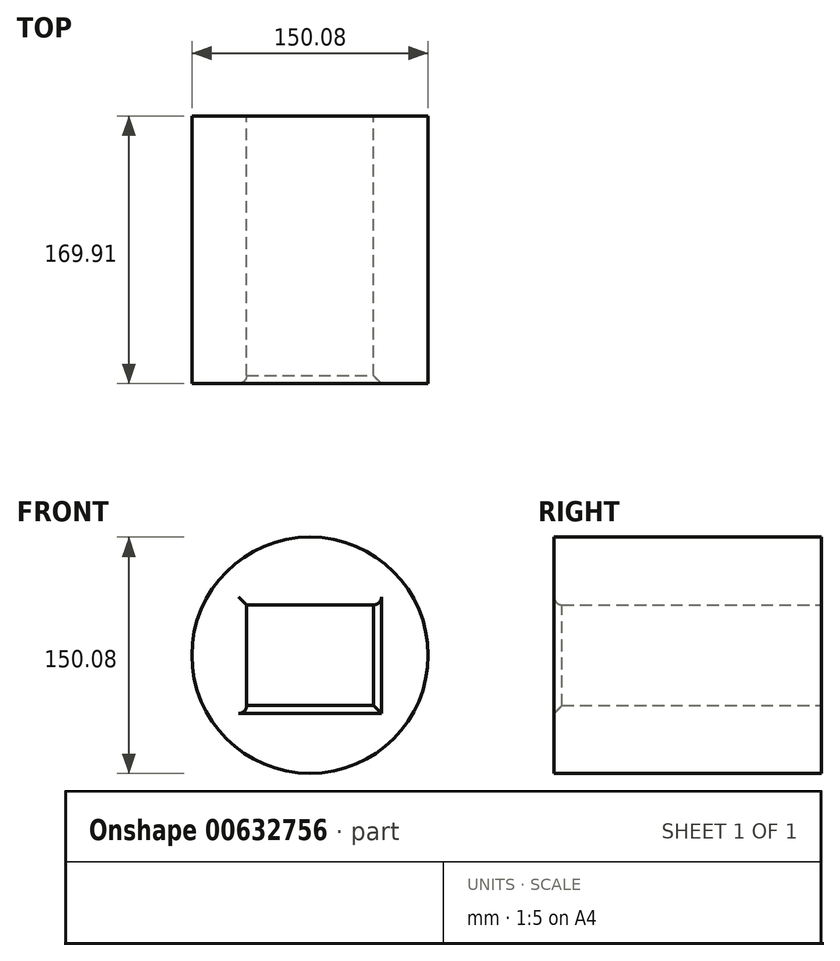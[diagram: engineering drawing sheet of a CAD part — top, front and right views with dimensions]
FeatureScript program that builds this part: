
annotation { "Feature Type Name" : "Feature", "Feature Type Description" : "" }
export const myFeature = defineFeature(function(context is Context, id is Id, definition is map)
    precondition{}
    {
        {
            var Q0;
            Q0=qCreatedBy(makeId("Front.planeOp"),FACE);
            var sketch = newSketch(context, id + "F0", { "sketchPlane" : qUnion([Q0])});
            skCircle(sketch, "E0", {"center": v(0, 0) * mm, "radius": 75.04 * mm});
            skLineSegment(sketch, "E1.bottom", {"start": v(40.33, -31.96) * mm, "end": v(-40.33, -31.96) * mm});
            skLineSegment(sketch, "E1.top", {"start": v(40.33, 31.96) * mm, "end": v(-40.33, 31.96) * mm});
            skLineSegment(sketch, "E1.left", {"start": v(40.33, -31.96) * mm, "end": v(40.33, 31.96) * mm});
            skLineSegment(sketch, "E1.right", {"start": v(-40.33, -31.96) * mm, "end": v(-40.33, 31.96) * mm});
            skSolve(sketch);
        }
        {
            var Q0;
            Q0 = qSketchRegion(id + "F0", true);
            extrude(context, id + "F1", {"entities" : qUnion([Q0]), "depth" : 169.9 * mm, "offsetDistance" : 25.4 * mm});
        }
        {
            var Q0;
            Q0=makeQuery(id+"F1.opExtrude","CAP_EDGE",EDGE,{"disambiguationData":[OSD([sQuery(id+"F0.wireOp",EDGE,"E1.top")])],"isStart":false});
            var Q1;
            Q1=makeQuery(id+"F1.opExtrude","CAP_EDGE",EDGE,{"disambiguationData":[OSD([sQuery(id+"F0.wireOp",EDGE,"E1.right")])],"isStart":false});
            fillet(context, id + "F2", {"entities" : qUnion([Q0, Q1]), "radius" : 5.08 * mm, "tangentPropagation" : true, "allowEdgeOverflow" : false});
        }
        {
            var Q0;
            Q0=makeQuery(id+"F1.opExtrude","CAP_EDGE",EDGE,{"disambiguationData":[OSD([sQuery(id+"F0.wireOp",EDGE,"E1.left")])],"isStart":false});
            var Q1;
            Q1=makeQuery(id+"F1.opExtrude","CAP_EDGE",EDGE,{"disambiguationData":[OSD([sQuery(id+"F0.wireOp",EDGE,"E1.bottom")])],"isStart":false});
            chamfer(context, id + "F3", {"entities" : qUnion([Q0, Q1]), "width" : 5.08 * mm, "tangentPropagation" : true});
        }
    });
